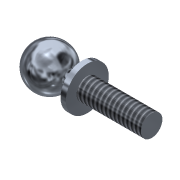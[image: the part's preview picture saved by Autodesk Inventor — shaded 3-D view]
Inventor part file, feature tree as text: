
AUTODESK INVENTOR PART (.ipt)
format: ipt  version: 2014 (Build 180170000, 170)  size: 134,656 bytes
history: native  units: in
note: dims shown in document units (in); Inventor stores cm internally (conversion verified against a paired STEP export)
features: revolve x1, thread x1, sketch x1
ambient origin geometry x8: Origin, YZ Plane, XZ Plane, XY Plane, X Axis, Y Axis, Z Axis, Center Point
bodies: Solid1 (feature_tree)
feature tree (3):
  revolve  "Revolution1"  [1 undecoded]
  thread  "Thread1"  [1 undecoded]
  sketch  "Sketch1"  dims[d0=0.05in d1=0.375in d3=0.5in d4=0.25in d5=0.5in d6=0.0625in d7=0.75in d8=90.0deg d9=1.0in d10=0.0in]
note: 2 required parameter values undecoded (feature->parameter linkage not recoverable at this tier; creation-order binding heuristic only, values carry confidence <= 0.55)